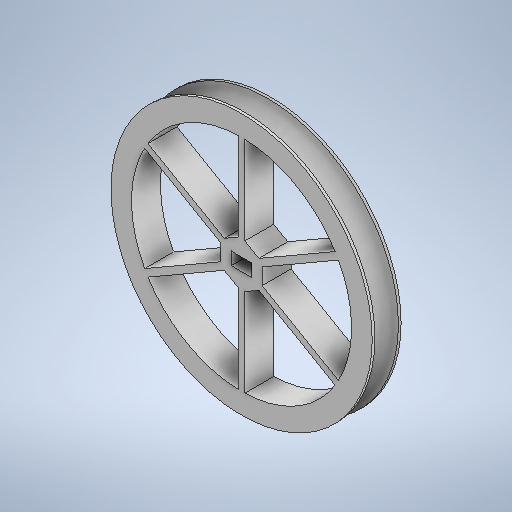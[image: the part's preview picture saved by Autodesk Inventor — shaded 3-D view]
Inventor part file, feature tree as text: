
AUTODESK INVENTOR PART (.ipt)
format: ipt  version: 2025.3 (Build 293356030, 356C)  size: 327,168 bytes
history: native  units: mm
features: sketch x4, extrude x3, other x1, pattern_circular x1
ambient origin geometry x8: Origin, YZ Plane, XZ Plane, XY Plane, X Axis, Y Axis, Z Axis, Center Point
bodies: Body1 (feature_tree)
feature tree (9):
  other  "ソリッド1"
  extrude  "ハブ"  Depth=7.0mm
  extrude  "スポーク"  Depth=5.0mm
  pattern_circular  "円形状パターン1"  Angle=90.0deg  [1 undecoded]
  extrude  "軸穴"  Depth=10.0mm TaperAngle=0.0deg
  sketch  "スケッチ1"
  sketch  "スケッチ3"
  sketch  "スケッチ4"
  sketch  "スケッチ5"
note: 1 required parameter value undecoded (feature->parameter linkage not recoverable at this tier; creation-order binding heuristic only, values carry confidence <= 0.55)
